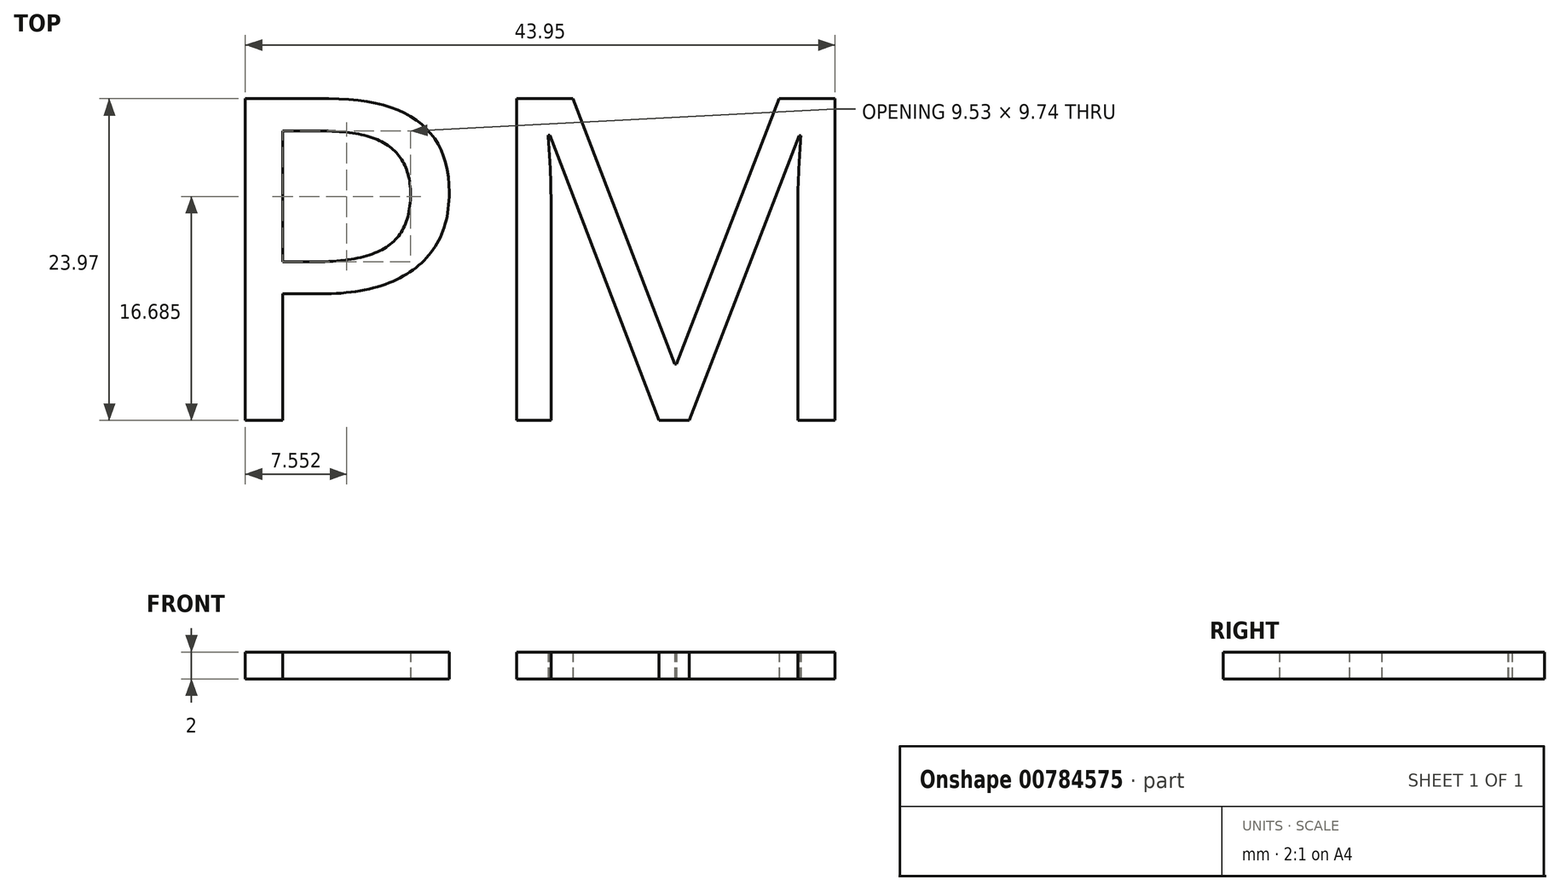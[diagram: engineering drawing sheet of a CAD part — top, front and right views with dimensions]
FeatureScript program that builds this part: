
annotation { "Feature Type Name" : "Feature", "Feature Type Description" : "" }
export const myFeature = defineFeature(function(context is Context, id is Id, definition is map)
    precondition{}
    {
        {
            var Q0;
            Q0=qCreatedBy(makeId("Top.planeOp"),FACE);
            var sketch = newSketch(context, id + "F0", { "sketchPlane" : qUnion([Q0])});
            skText(sketch, "E0", { "text": "PM\n", "fontName": "OpenSans-Regular.ttf"});
            const initialGuessF0  = {"E0": [-0.04315, -0.06928, 1, 0, 0.02417]};
            skSetInitialGuess(sketch, initialGuessF0);
            skSolve(sketch);
        }
        {
            var Q0;
            Q0 = qSketchRegion(id + "F0", true);
            extrude(context, id + "F1", {"entities" : qUnion([Q0]), "depth" : 2 * mm, "offsetDistance" : 25 * mm});
        }
    });
